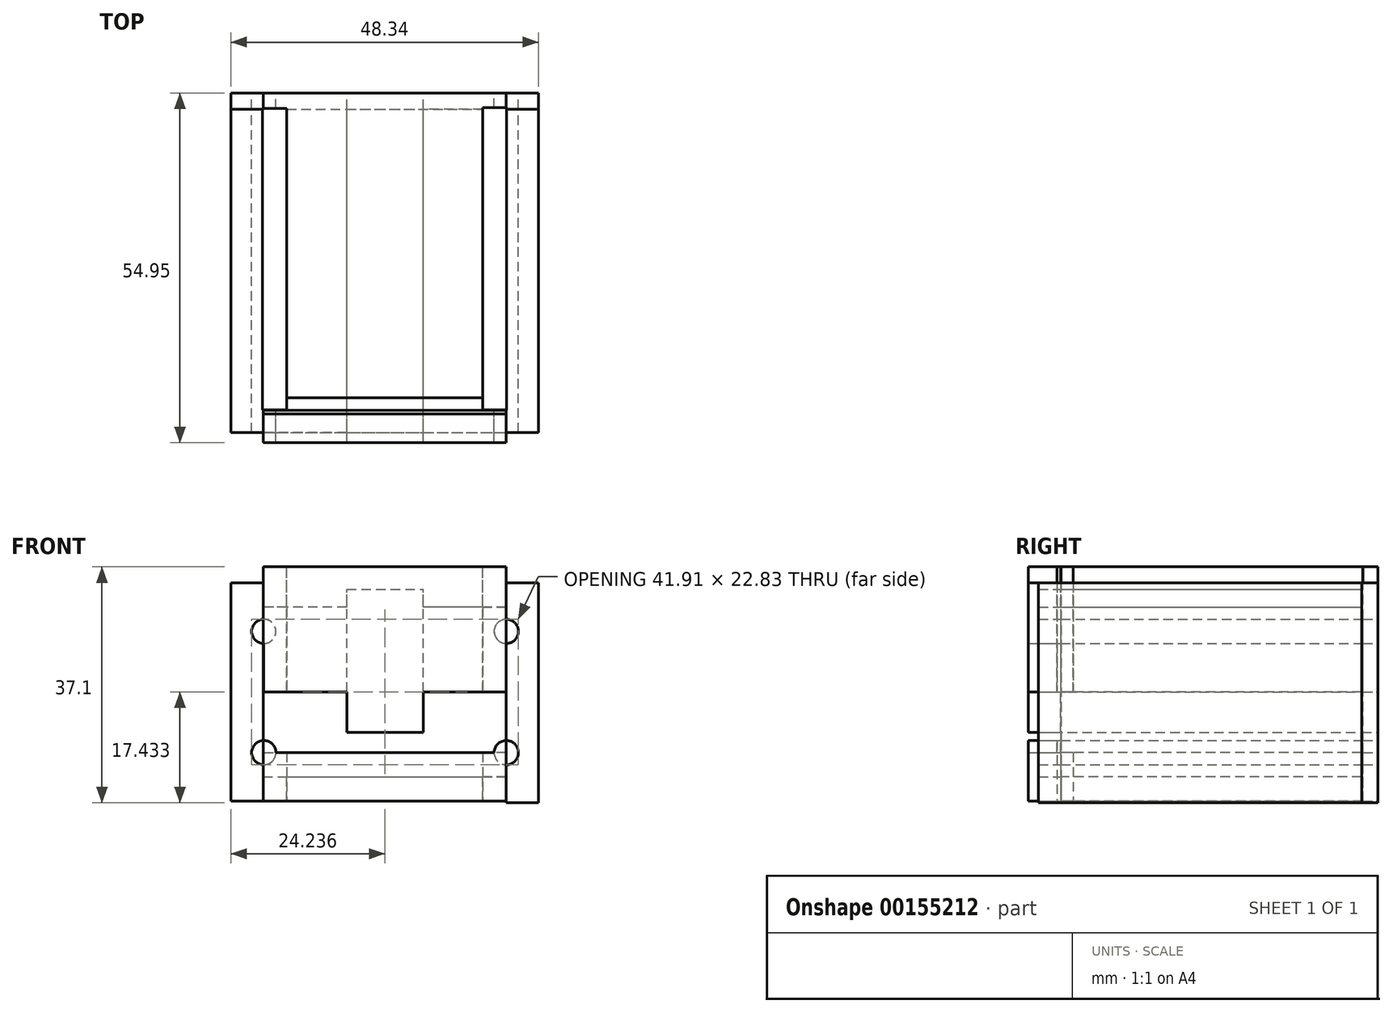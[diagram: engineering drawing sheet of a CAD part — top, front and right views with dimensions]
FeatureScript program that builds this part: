
annotation { "Feature Type Name" : "Feature", "Feature Type Description" : "" }
export const myFeature = defineFeature(function(context is Context, id is Id, definition is map)
    precondition{}
    {
        {
            var Q0;
            Q0=qCreatedBy(makeId("Front.planeOp"),FACE);
            var sketch = newSketch(context, id + "F0", { "sketchPlane" : qUnion([Q0])});
            skLineSegment(sketch, "E0.bottom", {"start": v(-20.46, 7.72) * mm, "end": v(17.64, 7.72) * mm});
            skLineSegment(sketch, "E0.top", {"start": v(-20.46, -11.33) * mm, "end": v(17.64, -11.33) * mm});
            skLineSegment(sketch, "E0.left", {"start": v(-20.46, 7.72) * mm, "end": v(-20.46, -11.33) * mm});
            skLineSegment(sketch, "E0.right", {"start": v(17.64, 7.72) * mm, "end": v(17.64, -11.33) * mm});
            skLineSegment(sketch, "E1.bottom", {"start": v(-20.56, 15.34) * mm, "end": v(17.62, 15.34) * mm});
            skLineSegment(sketch, "E1.top", {"start": v(-20.56, -18.95) * mm, "end": v(17.62, -18.95) * mm});
            skLineSegment(sketch, "E1.left", {"start": v(-20.56, 15.34) * mm, "end": v(-20.56, -18.95) * mm});
            skLineSegment(sketch, "E1.right", {"start": v(17.62, 15.34) * mm, "end": v(17.62, -18.95) * mm});
            skLineSegment(sketch, "E2.bottom", {"start": v(17.62, 15.34) * mm, "end": v(-20.56, 15.34) * mm});
            skLineSegment(sketch, "E2.top", {"start": v(17.62, 11.53) * mm, "end": v(-20.56, 11.53) * mm});
            skLineSegment(sketch, "E2.left", {"start": v(17.62, 15.34) * mm, "end": v(17.62, 11.53) * mm});
            skLineSegment(sketch, "E2.right", {"start": v(-20.56, 15.34) * mm, "end": v(-20.56, 11.53) * mm});
            skLineSegment(sketch, "E3.top", {"start": v(-20.56, -15.14) * mm, "end": v(17.62, -15.14) * mm});
            skLineSegment(sketch, "E3.left", {"start": v(-20.56, -18.95) * mm, "end": v(-20.56, -15.14) * mm});
            skLineSegment(sketch, "E3.right", {"start": v(17.62, -18.95) * mm, "end": v(17.62, -15.14) * mm});
            skLineSegment(sketch, "E4.bottom", {"start": v(17.62, 15.34) * mm, "end": v(22.7, 15.34) * mm});
            skLineSegment(sketch, "E4.top", {"start": v(17.62, -19.22) * mm, "end": v(22.7, -19.22) * mm});
            skLineSegment(sketch, "E4.left", {"start": v(17.62, 15.34) * mm, "end": v(17.62, -19.22) * mm});
            skLineSegment(sketch, "E4.right", {"start": v(22.7, 15.34) * mm, "end": v(22.7, -19.22) * mm});
            skLineSegment(sketch, "E5.bottom", {"start": v(-20.56, 15.34) * mm, "end": v(-25.64, 15.34) * mm});
            skLineSegment(sketch, "E5.top", {"start": v(-20.56, -18.94) * mm, "end": v(-25.64, -18.94) * mm});
            skLineSegment(sketch, "E5.left", {"start": v(-20.56, 15.34) * mm, "end": v(-20.56, -18.94) * mm});
            skLineSegment(sketch, "E5.right", {"start": v(-25.64, 15.34) * mm, "end": v(-25.64, -18.94) * mm});
            skCircle(sketch, "E6", {"center": v(-20.46, 7.72) * mm, "radius": 1.9 * mm});
            skCircle(sketch, "E7", {"center": v(-20.46, -11.33) * mm, "radius": 1.9 * mm});
            skCircle(sketch, "E8", {"center": v(17.64, -11.33) * mm, "radius": 1.9 * mm});
            skCircle(sketch, "E9", {"center": v(17.64, 7.72) * mm, "radius": 1.9 * mm});
            skLineSegment(sketch, "E10.bottom", {"start": v(4.92, -23.75) * mm, "end": v(-7.86, -23.75) * mm});
            skLineSegment(sketch, "E10.top", {"start": v(4.92, -18.95) * mm, "end": v(-7.86, -18.95) * mm});
            skLineSegment(sketch, "E10.left", {"start": v(4.92, -23.75) * mm, "end": v(4.92, -18.95) * mm});
            skLineSegment(sketch, "E10.right", {"start": v(-7.86, -23.75) * mm, "end": v(-7.86, -18.95) * mm});
            skCircle(sketch, "E11", {"center": v(-1.47, -23.75) * mm, "radius": 2.38 * mm});
            skLineSegment(sketch, "E12", {"start": v(-20.46, -1.8) * mm, "end": v(17.64, -1.8) * mm});
            skLineSegment(sketch, "E13", {"start": v(-1.4, -1.8) * mm, "end": v(-1.4, -11.33) * mm});
            skLineSegment(sketch, "E14", {"start": v(-1.4, -11.33) * mm, "end": v(-1.4, 7.72) * mm});
            skLineSegment(sketch, "E15", {"start": v(-7.42, -8.15) * mm, "end": v(4.58, -8.15) * mm});
            skLineSegment(sketch, "E16", {"start": v(-7.42, -8.15) * mm, "end": v(-7.42, 14.35) * mm});
            skLineSegment(sketch, "E17", {"start": v(4.58, -8.15) * mm, "end": v(4.58, 14.35) * mm});
            skLineSegment(sketch, "E18", {"start": v(-7.42, 14.35) * mm, "end": v(4.58, 14.35) * mm});
            skLineSegment(sketch, "E19.bottom", {"start": v(-20.56, 15.34) * mm, "end": v(17.63, 15.34) * mm});
            skLineSegment(sketch, "E19.top", {"start": v(-20.56, 17.88) * mm, "end": v(17.63, 17.88) * mm});
            skLineSegment(sketch, "E19.left", {"start": v(-20.56, 15.34) * mm, "end": v(-20.56, 17.88) * mm});
            skLineSegment(sketch, "E19.right", {"start": v(17.63, 15.34) * mm, "end": v(17.63, 17.88) * mm});
            skSolve(sketch);
        }
        {
            var Q0;
            Q0=makeQuery(id+"F0.imprint","IMPRINT",FACE,{"disambiguationData":[TD([[makeQuery(id+"F0.imprint","IMPRINT",EDGE,{"derivedFrom":sQuery(id+"F0.wireOp",EDGE,"E10.top")}),1.0]])]});
            var Q1;
            {var subQ0=sQuery(id+"F0.wireOp",EDGE,"E2.bottom");Q1=makeQuery(id+"F0.imprint","IMPRINT",FACE,{"disambiguationData":[TD([[makeQuery(id+"F0.imprint","IMPRINT",EDGE,{"derivedFrom":subQ0}),1.0]])]});}
            var Q2;
            {var subQ5=sQuery(id+"F0.wireOp",EDGE,"E3.top");Q2=makeQuery(id+"F0.imprint","IMPRINT",FACE,{"disambiguationData":[TD([[makeQuery(id+"F0.imprint","IMPRINT",EDGE,{"derivedFrom":subQ5}),-1.0]])]});}
            var Q3;
            {var subQ12=sQuery(id+"F0.wireOp",EDGE,"E4.bottom");Q3=makeQuery(id+"F0.imprint","IMPRINT",FACE,{"disambiguationData":[TD([[makeQuery(id+"F0.imprint","IMPRINT",EDGE,{"derivedFrom":subQ12}),-1.0]])]});}
            var Q4;
            {var subQ1=sQuery(id+"F0.wireOp",EDGE,"E5.bottom");Q4=makeQuery(id+"F0.imprint","IMPRINT",FACE,{"disambiguationData":[TD([[makeQuery(id+"F0.imprint","IMPRINT",EDGE,{"derivedFrom":subQ1}),1.0]])]});}
            var Q5;
            {var subQ1=sQuery(id+"F0.wireOp",EDGE,"E2.top");Q5=makeQuery(id+"F0.imprint","IMPRINT",FACE,{"disambiguationData":[TD([[makeQuery(id+"F0.imprint","IMPRINT",EDGE,{"derivedFrom":subQ1}),1.0]])]});}
            var Q6;
            Q6=makeQuery(id+"F0.imprint","IMPRINT",FACE,{"disambiguationData":[TD([[makeQuery(id+"F0.imprint","IMPRINT",EDGE,{"derivedFrom":sQuery(id+"F0.wireOp",EDGE,"04iNWCrk-ZHZP-uxNH-fGxF-0B0Pyckvw0wm")}),-1.0]])]});
            var Q7;
            Q7=makeQuery(id+"F0.imprint","IMPRINT",FACE,{"disambiguationData":[TD([[makeQuery(id+"F0.imprint","IMPRINT",EDGE,{"derivedFrom":sQuery(id+"F0.wireOp",EDGE,"04iNWCrk-ZHZP-uxNH-fGxF-0B0Pyckvw0wm")}),1.0]])]});
            var Q8;
            {var subQ1=sQuery(id+"F0.wireOp",EDGE,"E3.top");Q8=makeQuery(id+"F0.imprint","IMPRINT",FACE,{"disambiguationData":[TD([[makeQuery(id+"F0.imprint","IMPRINT",EDGE,{"derivedFrom":subQ1}),1.0]])]});}
            var Q9;
            {var subQ0=sQuery(id+"F0.wireOp",EDGE,"E6");var subQ1=sQuery(id+"F0.wireOp",EDGE,"E0.bottom");var subQ2=makeQuery(id+"F0.imprint","INTERSECT",VERTEX,{"derivedFrom":[subQ1,subQ0]});Q9=makeQuery(id+"F0.imprint","IMPRINT",FACE,{"disambiguationData":[TD([[makeQuery(id+"F0.imprint","IMPRINT",EDGE,{"disambiguationData":[TD([[subQ2,-1.0]])],"derivedFrom":subQ1}),-1.0]])]});}
            var Q10;
            {var subQ0=sQuery(id+"F0.wireOp",EDGE,"E14");var subQ1=sQuery(id+"F0.wireOp",EDGE,"E0.bottom");var subQ2=makeQuery(id+"F0.imprint","INTERSECT",VERTEX,{"derivedFrom":[subQ1,subQ0]});Q10=makeQuery(id+"F0.imprint","IMPRINT",FACE,{"disambiguationData":[TD([[makeQuery(id+"F0.imprint","IMPRINT",EDGE,{"disambiguationData":[TD([[subQ2,1.0]])],"derivedFrom":subQ1}),-1.0]])]});}
            var Q11;
            {var subQ0=sQuery(id+"F0.wireOp",EDGE,"E14");var subQ1=sQuery(id+"F0.wireOp",EDGE,"E0.bottom");var subQ2=makeQuery(id+"F0.imprint","INTERSECT",VERTEX,{"derivedFrom":[subQ1,subQ0]});Q11=makeQuery(id+"F0.imprint","IMPRINT",FACE,{"disambiguationData":[TD([[makeQuery(id+"F0.imprint","IMPRINT",EDGE,{"disambiguationData":[TD([[subQ2,-1.0]])],"derivedFrom":subQ1}),-1.0]])]});}
            var Q12;
            {var subQ8=sQuery(id+"F0.wireOp",EDGE,"E0.top");var subQ11=sQuery(id+"F0.wireOp",EDGE,"E14");var subQ12=makeQuery(id+"F0.imprint","INTERSECT",VERTEX,{"derivedFrom":[subQ8,subQ11]});Q12=makeQuery(id+"F0.imprint","IMPRINT",FACE,{"disambiguationData":[TD([[makeQuery(id+"F0.imprint","IMPRINT",EDGE,{"disambiguationData":[TD([[subQ12,-1.0]])],"derivedFrom":subQ8}),1.0]])]});}
            var Q13;
            {var subQ6=sQuery(id+"F0.wireOp",EDGE,"E0.top");var subQ11=sQuery(id+"F0.wireOp",EDGE,"E14");var subQ13=makeQuery(id+"F0.imprint","INTERSECT",VERTEX,{"derivedFrom":[subQ6,subQ11]});Q13=makeQuery(id+"F0.imprint","IMPRINT",FACE,{"disambiguationData":[TD([[makeQuery(id+"F0.imprint","IMPRINT",EDGE,{"disambiguationData":[TD([[subQ13,1.0]])],"derivedFrom":subQ6}),1.0]])]});}
            var Q14;
            {var subQ0=sQuery(id+"F0.wireOp",EDGE,"E16");var subQ1=sQuery(id+"F0.wireOp",EDGE,"E12");var subQ2=makeQuery(id+"F0.imprint","INTERSECT",VERTEX,{"derivedFrom":[subQ1,subQ0]});Q14=makeQuery(id+"F0.imprint","IMPRINT",FACE,{"disambiguationData":[TD([[makeQuery(id+"F0.imprint","IMPRINT",EDGE,{"disambiguationData":[TD([[subQ2,-1.0]])],"derivedFrom":subQ1}),-1.0]])]});}
            var Q15;
            {var subQ0=sQuery(id+"F0.wireOp",EDGE,"E14");var subQ1=sQuery(id+"F0.wireOp",EDGE,"E12");var subQ2=makeQuery(id+"F0.imprint","INTERSECT",VERTEX,{"derivedFrom":[subQ1,subQ0]});Q15=makeQuery(id+"F0.imprint","IMPRINT",FACE,{"disambiguationData":[TD([[makeQuery(id+"F0.imprint","IMPRINT",EDGE,{"disambiguationData":[TD([[subQ2,-1.0]])],"derivedFrom":subQ1}),-1.0]])]});}
            var Q16;
            {var subQ1=sQuery(id+"F0.wireOp",EDGE,"E0.bottom");var subQ7=sQuery(id+"F0.wireOp",EDGE,"E17");var subQ9=makeQuery(id+"F0.imprint","INTERSECT",VERTEX,{"derivedFrom":[subQ1,subQ7]});Q16=makeQuery(id+"F0.imprint","IMPRINT",FACE,{"disambiguationData":[TD([[makeQuery(id+"F0.imprint","IMPRINT",EDGE,{"disambiguationData":[TD([[subQ9,-1.0]])],"derivedFrom":subQ1}),-1.0]])]});}
            var Q17;
            {var subQ5=sQuery(id+"F0.wireOp",EDGE,"E18");Q17=makeQuery(id+"F0.imprint","IMPRINT",FACE,{"disambiguationData":[TD([[makeQuery(id+"F0.imprint","IMPRINT",EDGE,{"derivedFrom":subQ5}),-1.0]])]});}
            var Q18;
            {var subQ12=sQuery(id+"F0.wireOp",EDGE,"E18");Q18=makeQuery(id+"F0.imprint","IMPRINT",FACE,{"disambiguationData":[TD([[makeQuery(id+"F0.imprint","IMPRINT",EDGE,{"derivedFrom":subQ12}),1.0]])]});}
            var Q19;
            Q19=makeQuery(id+"F0.imprint","IMPRINT",FACE,{"disambiguationData":[TD([[makeQuery(id+"F0.imprint","IMPRINT",EDGE,{"derivedFrom":sQuery(id+"F0.wireOp",EDGE,"E19.top")}),-1.0]])]});
            extrude(context, id + "F1", {"entities" : qUnion([Q0, Q1, Q2, Q3, Q4, Q5, Q6, Q7, Q8, Q9, Q10, Q11, Q12, Q13, Q14, Q15, Q16, Q17, Q18, Q19]), "depth" : 2.54 * mm});
        }
        {
            var Q0;
            {var subQ0=sQuery(id+"F0.wireOp",EDGE,"E2.bottom");Q0=makeQuery(id+"F0.imprint","IMPRINT",FACE,{"disambiguationData":[TD([[makeQuery(id+"F0.imprint","IMPRINT",EDGE,{"derivedFrom":subQ0}),1.0]])]});}
            var Q1;
            {var subQ1=sQuery(id+"F0.wireOp",EDGE,"E1.top");Q1=makeQuery(id+"F0.imprint","IMPRINT",FACE,{"disambiguationData":[TD([[makeQuery(id+"F0.imprint","IMPRINT",EDGE,{"derivedFrom":subQ1}),1.0]])]});}
            var Q2;
            {var subQ12=sQuery(id+"F0.wireOp",EDGE,"E18");Q2=makeQuery(id+"F0.imprint","IMPRINT",FACE,{"disambiguationData":[TD([[makeQuery(id+"F0.imprint","IMPRINT",EDGE,{"derivedFrom":subQ12}),1.0]])]});}
            var Q3;
            Q3=makeQuery(id+"F0.imprint","IMPRINT",FACE,{"disambiguationData":[TD([[makeQuery(id+"F0.imprint","IMPRINT",EDGE,{"derivedFrom":sQuery(id+"F0.wireOp",EDGE,"E19.top")}),-1.0]])]});
            extrude(context, id + "F2", {"entities" : qUnion([Q0, Q1, Q2, Q3]), "operationType" : NewBodyOperationType.ADD, "depth" : 49.87 * mm, "hasSecondDirection" : true, "secondDirectionOppositeDirection" : false, "secondDirectionDepth" : 2.54 * mm});
        }
        {
            var Q0;
            {var subQ0=sQuery(id+"F0.wireOp",EDGE,"E2.bottom");Q0=makeQuery(id+"F0.imprint","IMPRINT",FACE,{"disambiguationData":[TD([[makeQuery(id+"F0.imprint","IMPRINT",EDGE,{"derivedFrom":subQ0}),1.0]])]});}
            var Q1;
            {var subQ1=sQuery(id+"F0.wireOp",EDGE,"E1.top");Q1=makeQuery(id+"F0.imprint","IMPRINT",FACE,{"disambiguationData":[TD([[makeQuery(id+"F0.imprint","IMPRINT",EDGE,{"derivedFrom":subQ1}),1.0]])]});}
            var Q2;
            {var subQ1=sQuery(id+"F0.wireOp",EDGE,"E2.top");Q2=makeQuery(id+"F0.imprint","IMPRINT",FACE,{"disambiguationData":[TD([[makeQuery(id+"F0.imprint","IMPRINT",EDGE,{"derivedFrom":subQ1}),1.0]])]});}
            var Q3;
            {var subQ4=sQuery(id+"F0.wireOp",EDGE,"E0.left");var subQ5=sQuery(id+"F0.wireOp",EDGE,"E0.bottom");var subQ6=makeQuery(id+"F0.imprint","INTERSECT",VERTEX,{"derivedFrom":[subQ5,subQ4]});Q3=makeQuery(id+"F0.imprint","IMPRINT",FACE,{"disambiguationData":[TD([[makeQuery(id+"F0.imprint","IMPRINT",EDGE,{"disambiguationData":[TD([[subQ6,-1.0]])],"derivedFrom":subQ5}),1.0]])]});}
            var Q4;
            Q4=makeQuery(id+"F0.imprint","IMPRINT",FACE,{"disambiguationData":[TD([[makeQuery(id+"F0.imprint","IMPRINT",EDGE,{"derivedFrom":sQuery(id+"F0.wireOp",EDGE,"04iNWCrk-ZHZP-uxNH-fGxF-0B0Pyckvw0wm")}),-1.0]])]});
            var Q5;
            {var subQ1=sQuery(id+"F0.wireOp",EDGE,"E3.top");Q5=makeQuery(id+"F0.imprint","IMPRINT",FACE,{"disambiguationData":[TD([[makeQuery(id+"F0.imprint","IMPRINT",EDGE,{"derivedFrom":subQ1}),1.0]])]});}
            var Q6;
            {var subQ0=sQuery(id+"F0.wireOp",EDGE,"E0.left");var subQ1=sQuery(id+"F0.wireOp",EDGE,"E0.top");var subQ2=makeQuery(id+"F0.imprint","INTERSECT",VERTEX,{"derivedFrom":[subQ1,subQ0]});Q6=makeQuery(id+"F0.imprint","IMPRINT",FACE,{"disambiguationData":[TD([[makeQuery(id+"F0.imprint","IMPRINT",EDGE,{"disambiguationData":[TD([[subQ2,-1.0]])],"derivedFrom":subQ1}),1.0]])]});}
            var Q7;
            {var subQ4=sQuery(id+"F0.wireOp",EDGE,"E0.left");var subQ5=sQuery(id+"F0.wireOp",EDGE,"E0.top");var subQ6=makeQuery(id+"F0.imprint","INTERSECT",VERTEX,{"derivedFrom":[subQ5,subQ4]});Q7=makeQuery(id+"F0.imprint","IMPRINT",FACE,{"disambiguationData":[TD([[makeQuery(id+"F0.imprint","IMPRINT",EDGE,{"disambiguationData":[TD([[subQ6,-1.0]])],"derivedFrom":subQ5}),-1.0]])]});}
            var Q8;
            {var subQ0=sQuery(id+"F0.wireOp",EDGE,"E8");var subQ1=sQuery(id+"F0.wireOp",EDGE,"E0.top");var subQ2=makeQuery(id+"F0.imprint","INTERSECT",VERTEX,{"derivedFrom":[subQ1,subQ0]});Q8=makeQuery(id+"F0.imprint","IMPRINT",FACE,{"disambiguationData":[TD([[makeQuery(id+"F0.imprint","IMPRINT",EDGE,{"disambiguationData":[TD([[subQ2,-1.0]])],"derivedFrom":subQ1}),-1.0]])]});}
            var Q9;
            {var subQ0=sQuery(id+"F0.wireOp",EDGE,"E8");var subQ1=sQuery(id+"F0.wireOp",EDGE,"E0.top");var subQ2=makeQuery(id+"F0.imprint","INTERSECT",VERTEX,{"derivedFrom":[subQ1,subQ0]});Q9=makeQuery(id+"F0.imprint","IMPRINT",FACE,{"disambiguationData":[TD([[makeQuery(id+"F0.imprint","IMPRINT",EDGE,{"disambiguationData":[TD([[subQ2,-1.0]])],"derivedFrom":subQ1}),1.0]])]});}
            var Q10;
            {var subQ0=sQuery(id+"F0.wireOp",EDGE,"E9");var subQ1=sQuery(id+"F0.wireOp",EDGE,"E0.bottom");var subQ2=makeQuery(id+"F0.imprint","INTERSECT",VERTEX,{"derivedFrom":[subQ1,subQ0]});Q10=makeQuery(id+"F0.imprint","IMPRINT",FACE,{"disambiguationData":[TD([[makeQuery(id+"F0.imprint","IMPRINT",EDGE,{"disambiguationData":[TD([[subQ2,-1.0]])],"derivedFrom":subQ1}),1.0]])]});}
            var Q11;
            {var subQ0=sQuery(id+"F0.wireOp",EDGE,"E9");var subQ1=sQuery(id+"F0.wireOp",EDGE,"E0.bottom");var subQ2=makeQuery(id+"F0.imprint","INTERSECT",VERTEX,{"derivedFrom":[subQ1,subQ0]});Q11=makeQuery(id+"F0.imprint","IMPRINT",FACE,{"disambiguationData":[TD([[makeQuery(id+"F0.imprint","IMPRINT",EDGE,{"disambiguationData":[TD([[subQ2,-1.0]])],"derivedFrom":subQ1}),-1.0]])]});}
            var Q12;
            Q12=makeQuery(id+"F0.imprint","IMPRINT",FACE,{"disambiguationData":[TD([[makeQuery(id+"F0.imprint","IMPRINT",EDGE,{"derivedFrom":sQuery(id+"F0.wireOp",EDGE,"04iNWCrk-ZHZP-uxNH-fGxF-0B0Pyckvw0wm")}),1.0]])]});
            var Q13;
            {var subQ0=sQuery(id+"F0.wireOp",EDGE,"E0.left");var subQ1=sQuery(id+"F0.wireOp",EDGE,"E0.bottom");var subQ2=makeQuery(id+"F0.imprint","INTERSECT",VERTEX,{"derivedFrom":[subQ1,subQ0]});Q13=makeQuery(id+"F0.imprint","IMPRINT",FACE,{"disambiguationData":[TD([[makeQuery(id+"F0.imprint","IMPRINT",EDGE,{"disambiguationData":[TD([[subQ2,-1.0]])],"derivedFrom":subQ1}),-1.0]])]});}
            var Q14;
            {var subQ3=sQuery(id+"F0.wireOp",EDGE,"E17");var subQ6=sQuery(id+"F0.wireOp",EDGE,"E0.bottom");var subQ9=makeQuery(id+"F0.imprint","INTERSECT",VERTEX,{"derivedFrom":[subQ6,subQ3]});Q14=makeQuery(id+"F0.imprint","IMPRINT",FACE,{"disambiguationData":[TD([[makeQuery(id+"F0.imprint","IMPRINT",EDGE,{"disambiguationData":[TD([[subQ9,-1.0]])],"derivedFrom":subQ6}),-1.0]])]});}
            var Q15;
            {var subQ12=sQuery(id+"F0.wireOp",EDGE,"E18");Q15=makeQuery(id+"F0.imprint","IMPRINT",FACE,{"disambiguationData":[TD([[makeQuery(id+"F0.imprint","IMPRINT",EDGE,{"derivedFrom":subQ12}),1.0]])]});}
            var Q16;
            {var subQ5=sQuery(id+"F0.wireOp",EDGE,"E18");Q16=makeQuery(id+"F0.imprint","IMPRINT",FACE,{"disambiguationData":[TD([[makeQuery(id+"F0.imprint","IMPRINT",EDGE,{"derivedFrom":subQ5}),-1.0]])]});}
            var Q17;
            {var subQ5=sQuery(id+"F0.wireOp",EDGE,"E6");var subQ7=sQuery(id+"F0.wireOp",EDGE,"E0.bottom");var subQ8=makeQuery(id+"F0.imprint","INTERSECT",VERTEX,{"derivedFrom":[subQ7,subQ5]});Q17=makeQuery(id+"F0.imprint","IMPRINT",FACE,{"disambiguationData":[TD([[makeQuery(id+"F0.imprint","IMPRINT",EDGE,{"disambiguationData":[TD([[subQ8,-1.0]])],"derivedFrom":subQ7}),-1.0]])]});}
            var Q18;
            {var subQ0=sQuery(id+"F0.wireOp",EDGE,"E14");var subQ1=sQuery(id+"F0.wireOp",EDGE,"E0.bottom");var subQ2=makeQuery(id+"F0.imprint","INTERSECT",VERTEX,{"derivedFrom":[subQ1,subQ0]});Q18=makeQuery(id+"F0.imprint","IMPRINT",FACE,{"disambiguationData":[TD([[makeQuery(id+"F0.imprint","IMPRINT",EDGE,{"disambiguationData":[TD([[subQ2,1.0]])],"derivedFrom":subQ1}),-1.0]])]});}
            var Q19;
            {var subQ8=sQuery(id+"F0.wireOp",EDGE,"E0.top");var subQ11=sQuery(id+"F0.wireOp",EDGE,"E14");var subQ12=makeQuery(id+"F0.imprint","INTERSECT",VERTEX,{"derivedFrom":[subQ8,subQ11]});Q19=makeQuery(id+"F0.imprint","IMPRINT",FACE,{"disambiguationData":[TD([[makeQuery(id+"F0.imprint","IMPRINT",EDGE,{"disambiguationData":[TD([[subQ12,-1.0]])],"derivedFrom":subQ8}),1.0]])]});}
            var Q20;
            {var subQ5=sQuery(id+"F0.wireOp",EDGE,"E14");var subQ6=sQuery(id+"F0.wireOp",EDGE,"E0.top");var subQ7=makeQuery(id+"F0.imprint","INTERSECT",VERTEX,{"derivedFrom":[subQ6,subQ5]});Q20=makeQuery(id+"F0.imprint","IMPRINT",FACE,{"disambiguationData":[TD([[makeQuery(id+"F0.imprint","IMPRINT",EDGE,{"disambiguationData":[TD([[subQ7,1.0]])],"derivedFrom":subQ6}),1.0]])]});}
            var Q21;
            {var subQ0=sQuery(id+"F0.wireOp",EDGE,"E16");var subQ1=sQuery(id+"F0.wireOp",EDGE,"E12");var subQ2=makeQuery(id+"F0.imprint","INTERSECT",VERTEX,{"derivedFrom":[subQ1,subQ0]});Q21=makeQuery(id+"F0.imprint","IMPRINT",FACE,{"disambiguationData":[TD([[makeQuery(id+"F0.imprint","IMPRINT",EDGE,{"disambiguationData":[TD([[subQ2,-1.0]])],"derivedFrom":subQ1}),-1.0]])]});}
            var Q22;
            {var subQ0=sQuery(id+"F0.wireOp",EDGE,"E14");var subQ1=sQuery(id+"F0.wireOp",EDGE,"E12");var subQ2=makeQuery(id+"F0.imprint","INTERSECT",VERTEX,{"derivedFrom":[subQ1,subQ0]});Q22=makeQuery(id+"F0.imprint","IMPRINT",FACE,{"disambiguationData":[TD([[makeQuery(id+"F0.imprint","IMPRINT",EDGE,{"disambiguationData":[TD([[subQ2,-1.0]])],"derivedFrom":subQ1}),-1.0]])]});}
            var Q23;
            {var subQ0=sQuery(id+"F0.wireOp",EDGE,"E14");var subQ1=sQuery(id+"F0.wireOp",EDGE,"E0.bottom");var subQ2=makeQuery(id+"F0.imprint","INTERSECT",VERTEX,{"derivedFrom":[subQ1,subQ0]});Q23=makeQuery(id+"F0.imprint","IMPRINT",FACE,{"disambiguationData":[TD([[makeQuery(id+"F0.imprint","IMPRINT",EDGE,{"disambiguationData":[TD([[subQ2,-1.0]])],"derivedFrom":subQ1}),-1.0]])]});}
            var Q24;
            Q24=makeQuery(id+"F0.imprint","IMPRINT",FACE,{"disambiguationData":[TD([[makeQuery(id+"F0.imprint","IMPRINT",EDGE,{"derivedFrom":sQuery(id+"F0.wireOp",EDGE,"E19.top")}),-1.0]])]});
            extrude(context, id + "F3", {"entities" : qUnion([Q0, Q1, Q2, Q3, Q4, Q5, Q6, Q7, Q8, Q9, Q10, Q11, Q12, Q13, Q14, Q15, Q16, Q17, Q18, Q19, Q20, Q21, Q22, Q23, Q24]), "depth" : 54.95 * mm, "hasSecondDirection" : true, "secondDirectionOppositeDirection" : false, "secondDirectionDepth" : 49.87 * mm});
        }
        {
            var Q0;
            Q0=makeQuery(id+"F0.imprint","IMPRINT",FACE,{"disambiguationData":[TD([[makeQuery(id+"F0.imprint","IMPRINT",EDGE,{"derivedFrom":sQuery(id+"F0.wireOp",EDGE,"04iNWCrk-ZHZP-uxNH-fGxF-0B0Pyckvw0wm")}),-1.0]])]});
            var Q1;
            {var subQ0=sQuery(id+"F0.wireOp",EDGE,"E0.left");var subQ1=sQuery(id+"F0.wireOp",EDGE,"E0.bottom");var subQ2=makeQuery(id+"F0.imprint","INTERSECT",VERTEX,{"derivedFrom":[subQ1,subQ0]});Q1=makeQuery(id+"F0.imprint","IMPRINT",FACE,{"disambiguationData":[TD([[makeQuery(id+"F0.imprint","IMPRINT",EDGE,{"disambiguationData":[TD([[subQ2,-1.0]])],"derivedFrom":subQ1}),-1.0]])]});}
            var Q2;
            {var subQ0=sQuery(id+"F0.wireOp",EDGE,"E0.left");var subQ1=sQuery(id+"F0.wireOp",EDGE,"E0.top");var subQ2=makeQuery(id+"F0.imprint","INTERSECT",VERTEX,{"derivedFrom":[subQ1,subQ0]});Q2=makeQuery(id+"F0.imprint","IMPRINT",FACE,{"disambiguationData":[TD([[makeQuery(id+"F0.imprint","IMPRINT",EDGE,{"disambiguationData":[TD([[subQ2,-1.0]])],"derivedFrom":subQ1}),1.0]])]});}
            var Q3;
            {var subQ0=sQuery(id+"F0.wireOp",EDGE,"E8");var subQ1=sQuery(id+"F0.wireOp",EDGE,"E0.top");var subQ2=makeQuery(id+"F0.imprint","INTERSECT",VERTEX,{"derivedFrom":[subQ1,subQ0]});Q3=makeQuery(id+"F0.imprint","IMPRINT",FACE,{"disambiguationData":[TD([[makeQuery(id+"F0.imprint","IMPRINT",EDGE,{"disambiguationData":[TD([[subQ2,-1.0]])],"derivedFrom":subQ1}),1.0]])]});}
            var Q4;
            {var subQ0=sQuery(id+"F0.wireOp",EDGE,"E9");var subQ1=sQuery(id+"F0.wireOp",EDGE,"E0.bottom");var subQ2=makeQuery(id+"F0.imprint","INTERSECT",VERTEX,{"derivedFrom":[subQ1,subQ0]});Q4=makeQuery(id+"F0.imprint","IMPRINT",FACE,{"disambiguationData":[TD([[makeQuery(id+"F0.imprint","IMPRINT",EDGE,{"disambiguationData":[TD([[subQ2,-1.0]])],"derivedFrom":subQ1}),-1.0]])]});}
            var Q5;
            {var subQ5=sQuery(id+"F0.wireOp",EDGE,"E6");var subQ7=sQuery(id+"F0.wireOp",EDGE,"E0.bottom");var subQ8=makeQuery(id+"F0.imprint","INTERSECT",VERTEX,{"derivedFrom":[subQ7,subQ5]});Q5=makeQuery(id+"F0.imprint","IMPRINT",FACE,{"disambiguationData":[TD([[makeQuery(id+"F0.imprint","IMPRINT",EDGE,{"disambiguationData":[TD([[subQ8,-1.0]])],"derivedFrom":subQ7}),-1.0]])]});}
            var Q6;
            {var subQ1=sQuery(id+"F0.wireOp",EDGE,"E0.bottom");var subQ7=sQuery(id+"F0.wireOp",EDGE,"E17");var subQ9=makeQuery(id+"F0.imprint","INTERSECT",VERTEX,{"derivedFrom":[subQ1,subQ7]});Q6=makeQuery(id+"F0.imprint","IMPRINT",FACE,{"disambiguationData":[TD([[makeQuery(id+"F0.imprint","IMPRINT",EDGE,{"disambiguationData":[TD([[subQ9,-1.0]])],"derivedFrom":subQ1}),1.0]])]});}
            var Q7;
            {var subQ3=sQuery(id+"F0.wireOp",EDGE,"E17");var subQ6=sQuery(id+"F0.wireOp",EDGE,"E0.bottom");var subQ9=makeQuery(id+"F0.imprint","INTERSECT",VERTEX,{"derivedFrom":[subQ6,subQ3]});Q7=makeQuery(id+"F0.imprint","IMPRINT",FACE,{"disambiguationData":[TD([[makeQuery(id+"F0.imprint","IMPRINT",EDGE,{"disambiguationData":[TD([[subQ9,-1.0]])],"derivedFrom":subQ6}),-1.0]])]});}
            var Q8;
            {var subQ8=sQuery(id+"F0.wireOp",EDGE,"E0.top");var subQ11=sQuery(id+"F0.wireOp",EDGE,"E14");var subQ12=makeQuery(id+"F0.imprint","INTERSECT",VERTEX,{"derivedFrom":[subQ8,subQ11]});Q8=makeQuery(id+"F0.imprint","IMPRINT",FACE,{"disambiguationData":[TD([[makeQuery(id+"F0.imprint","IMPRINT",EDGE,{"disambiguationData":[TD([[subQ12,-1.0]])],"derivedFrom":subQ8}),1.0]])]});}
            var Q9;
            {var subQ5=sQuery(id+"F0.wireOp",EDGE,"E14");var subQ6=sQuery(id+"F0.wireOp",EDGE,"E0.top");var subQ7=makeQuery(id+"F0.imprint","INTERSECT",VERTEX,{"derivedFrom":[subQ6,subQ5]});Q9=makeQuery(id+"F0.imprint","IMPRINT",FACE,{"disambiguationData":[TD([[makeQuery(id+"F0.imprint","IMPRINT",EDGE,{"disambiguationData":[TD([[subQ7,1.0]])],"derivedFrom":subQ6}),1.0]])]});}
            var Q10;
            {var subQ12=sQuery(id+"F0.wireOp",EDGE,"E18");Q10=makeQuery(id+"F0.imprint","IMPRINT",FACE,{"disambiguationData":[TD([[makeQuery(id+"F0.imprint","IMPRINT",EDGE,{"derivedFrom":subQ12}),1.0]])]});}
            var Q11;
            Q11=makeQuery(id+"F0.imprint","IMPRINT",FACE,{"disambiguationData":[TD([[makeQuery(id+"F0.imprint","IMPRINT",EDGE,{"derivedFrom":sQuery(id+"F0.wireOp",EDGE,"E19.top")}),-1.0]])]});
            var Q12;
            {var subQ3=sQuery(id+"F0.wireOp",EDGE,"E6");var subQ7=sQuery(id+"F0.wireOp",EDGE,"E0.bottom");var subQ8=makeQuery(id+"F0.imprint","INTERSECT",VERTEX,{"derivedFrom":[subQ7,subQ3]});Q12=makeQuery(id+"F0.imprint","IMPRINT",FACE,{"disambiguationData":[TD([[makeQuery(id+"F0.imprint","IMPRINT",EDGE,{"disambiguationData":[TD([[subQ8,-1.0]])],"derivedFrom":subQ7}),1.0]])]});}
            var Q13;
            {var subQ1=sQuery(id+"F0.wireOp",EDGE,"E0.bottom");var subQ6=sQuery(id+"F0.wireOp",EDGE,"E0.left");var subQ7=makeQuery(id+"F0.imprint","INTERSECT",VERTEX,{"derivedFrom":[subQ1,subQ6]});Q13=makeQuery(id+"F0.imprint","IMPRINT",FACE,{"disambiguationData":[TD([[makeQuery(id+"F0.imprint","IMPRINT",EDGE,{"disambiguationData":[TD([[subQ7,-1.0]])],"derivedFrom":subQ1}),1.0]])]});}
            var Q14;
            {var subQ0=sQuery(id+"F0.wireOp",EDGE,"E9");var subQ1=sQuery(id+"F0.wireOp",EDGE,"E0.bottom");var subQ2=makeQuery(id+"F0.imprint","INTERSECT",VERTEX,{"derivedFrom":[subQ1,subQ0]});Q14=makeQuery(id+"F0.imprint","IMPRINT",FACE,{"disambiguationData":[TD([[makeQuery(id+"F0.imprint","IMPRINT",EDGE,{"disambiguationData":[TD([[subQ2,-1.0]])],"derivedFrom":subQ1}),1.0]])]});}
            var Q15;
            {var subQ5=sQuery(id+"F0.wireOp",EDGE,"E3.top");Q15=makeQuery(id+"F0.imprint","IMPRINT",FACE,{"disambiguationData":[TD([[makeQuery(id+"F0.imprint","IMPRINT",EDGE,{"derivedFrom":subQ5}),-1.0]])]});}
            var Q16;
            {var subQ0=sQuery(id+"F0.wireOp",EDGE,"E3.top");Q16=makeQuery(id+"F0.imprint","IMPRINT",FACE,{"disambiguationData":[TD([[makeQuery(id+"F0.imprint","IMPRINT",EDGE,{"derivedFrom":subQ0}),1.0]])]});}
            var Q17;
            {var subQ0=sQuery(id+"F0.wireOp",EDGE,"E8");var subQ1=sQuery(id+"F0.wireOp",EDGE,"E0.top");var subQ2=makeQuery(id+"F0.imprint","INTERSECT",VERTEX,{"derivedFrom":[subQ1,subQ0]});Q17=makeQuery(id+"F0.imprint","IMPRINT",FACE,{"disambiguationData":[TD([[makeQuery(id+"F0.imprint","IMPRINT",EDGE,{"disambiguationData":[TD([[subQ2,-1.0]])],"derivedFrom":subQ1}),-1.0]])]});}
            var Q18;
            {var subQ1=sQuery(id+"F0.wireOp",EDGE,"E0.left");var subQ6=sQuery(id+"F0.wireOp",EDGE,"E0.top");var subQ7=makeQuery(id+"F0.imprint","INTERSECT",VERTEX,{"derivedFrom":[subQ6,subQ1]});Q18=makeQuery(id+"F0.imprint","IMPRINT",FACE,{"disambiguationData":[TD([[makeQuery(id+"F0.imprint","IMPRINT",EDGE,{"disambiguationData":[TD([[subQ7,-1.0]])],"derivedFrom":subQ6}),-1.0]])]});}
            var Q19;
            Q19=makeQuery(id+"F0.imprint","IMPRINT",FACE,{"disambiguationData":[TD([[makeQuery(id+"F0.imprint","IMPRINT",EDGE,{"derivedFrom":sQuery(id+"F0.wireOp",EDGE,"E10.top")}),1.0]])]});
            extrude(context, id + "F4", {"entities" : qUnion([Q0, Q1, Q2, Q3, Q4, Q5, Q6, Q7, Q8, Q9, Q10, Q11, Q12, Q13, Q14, Q15, Q16, Q17, Q18, Q19]), "depth" : 50.43 * mm, "hasSecondDirection" : true, "secondDirectionOppositeDirection" : false, "secondDirectionDepth" : 47.9 * mm});
        }
        {
            var Q0;
            {var subQ0=sQuery(id+"F0.wireOp",EDGE,"E10.left");var subQ1=sQuery(id+"F0.wireOp",EDGE,"E10.bottom");var subQ2=sQuery(id+"F0.wireOp",EDGE,"E11");var subQ3=sQuery(id+"F0.wireOp",EDGE,"E4.left");var subQ4=sQuery(id+"F0.wireOp",EDGE,"E1.top");var subQ6=sQuery(id+"F0.wireOp",EDGE,"E10.right");var subQ7=sQuery(id+"F0.wireOp",EDGE,"E3.left");Q0=makeQuery(id+"F2.boolean.opBoolean","SPLIT",FACE,{"disambiguationData":[TD([makeQuery(id+"F1.opExtrude","SWEPT_FACE",FACE,{"disambiguationData":[OSD([subQ0])]})])],"derivedFrom":makeQuery(id+"F1.opExtrude","CAP_FACE",FACE,{"disambiguationData":[OSD([sQuery(id+"F0.wireOp",EDGE,"E0.left"),sQuery(id+"F0.wireOp",EDGE,"E0.right"),sQuery(id+"F0.wireOp",EDGE,"E2.bottom"),subQ4,subQ7,sQuery(id+"F0.wireOp",EDGE,"E4.bottom"),sQuery(id+"F0.wireOp",EDGE,"E4.top"),subQ3,sQuery(id+"F0.wireOp",EDGE,"E4.right"),sQuery(id+"F0.wireOp",EDGE,"E5.bottom"),sQuery(id+"F0.wireOp",EDGE,"E5.top"),sQuery(id+"F0.wireOp",EDGE,"E5.left"),sQuery(id+"F0.wireOp",EDGE,"E5.right"),sQuery(id+"F0.wireOp",EDGE,"E6"),sQuery(id+"F0.wireOp",EDGE,"E7"),sQuery(id+"F0.wireOp",EDGE,"E8"),sQuery(id+"F0.wireOp",EDGE,"E9"),subQ1,subQ0,subQ6,subQ2])],"isStart":false})});}
            extrude(context, id + "F5", {"entities" : qUnion([Q0]), "depth" : 50.8 * mm});
        }
        {
            var Q0;
            Q0=qCreatedBy(makeId("Top.planeOp"),FACE);
            var sketch = newSketch(context, id + "F6", { "sketchPlane" : qUnion([Q0])});
            skLineSegment(sketch, "E20.bottom", {"start": v(17.7, -2.33) * mm, "end": v(13.92, -2.33) * mm});
            skLineSegment(sketch, "E20.top", {"start": v(17.7, -49.8) * mm, "end": v(13.92, -49.8) * mm});
            skLineSegment(sketch, "E20.left", {"start": v(17.7, -2.33) * mm, "end": v(17.7, -49.8) * mm});
            skLineSegment(sketch, "E20.right", {"start": v(13.92, -2.33) * mm, "end": v(13.92, -49.8) * mm});
            skLineSegment(sketch, "E21.bottom", {"start": v(-20.65, -2.45) * mm, "end": v(-16.86, -2.45) * mm});
            skLineSegment(sketch, "E21.top", {"start": v(-20.65, -49.8) * mm, "end": v(-16.86, -49.8) * mm});
            skLineSegment(sketch, "E21.left", {"start": v(-20.65, -2.45) * mm, "end": v(-20.65, -49.8) * mm});
            skLineSegment(sketch, "E21.right", {"start": v(-16.86, -2.45) * mm, "end": v(-16.86, -49.8) * mm});
            skSolve(sketch);
        }
        {
            var Q0;
            Q0 = qSketchRegion(id + "F6", true);
            extrude(context, id + "F7", {"entities" : qUnion([Q0]), "operationType" : NewBodyOperationType.REMOVE, "oppositeDirection" : true, "depth" : 25.4 * mm, "hasSecondDirection" : true, "secondDirectionOppositeDirection" : false, "secondDirectionDepth" : 25.4 * mm});
        }
    });
